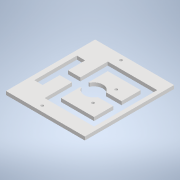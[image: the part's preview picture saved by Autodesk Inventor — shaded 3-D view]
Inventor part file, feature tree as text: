
AUTODESK INVENTOR PART (.ipt)
format: ipt  version: 2021 (Build 250183000, 183)  size: 144,384 bytes
history: native  units: mm
features: other x5, reference x2, extrude x1, sketch x1
ambient origin geometry x8: Origin, YZ Plane, XZ Plane, XY Plane, X Axis, Y Axis, Z Axis, Center Point
bodies: Body1 (feature_tree)
feature tree (9):
  other  "Sólido1"
  extrude  "Extrusión1"  Depth=10.0mm
  sketch  "Boceto1"  dims[d0=2.0mm d1=2.0mm d2=2.0mm d3=10.0mm d4=0.0mm]
  reference  "Referencia1"
  reference  "Referencia2"
  other  "<userpath>\OneDrive\Robotica\Proyecto-Rob\Piezas\Ensamble1.iam"
  other  "Ensamble1.iam"
  other  "TablaBase:1"
  other  "BaseGripper:1"
